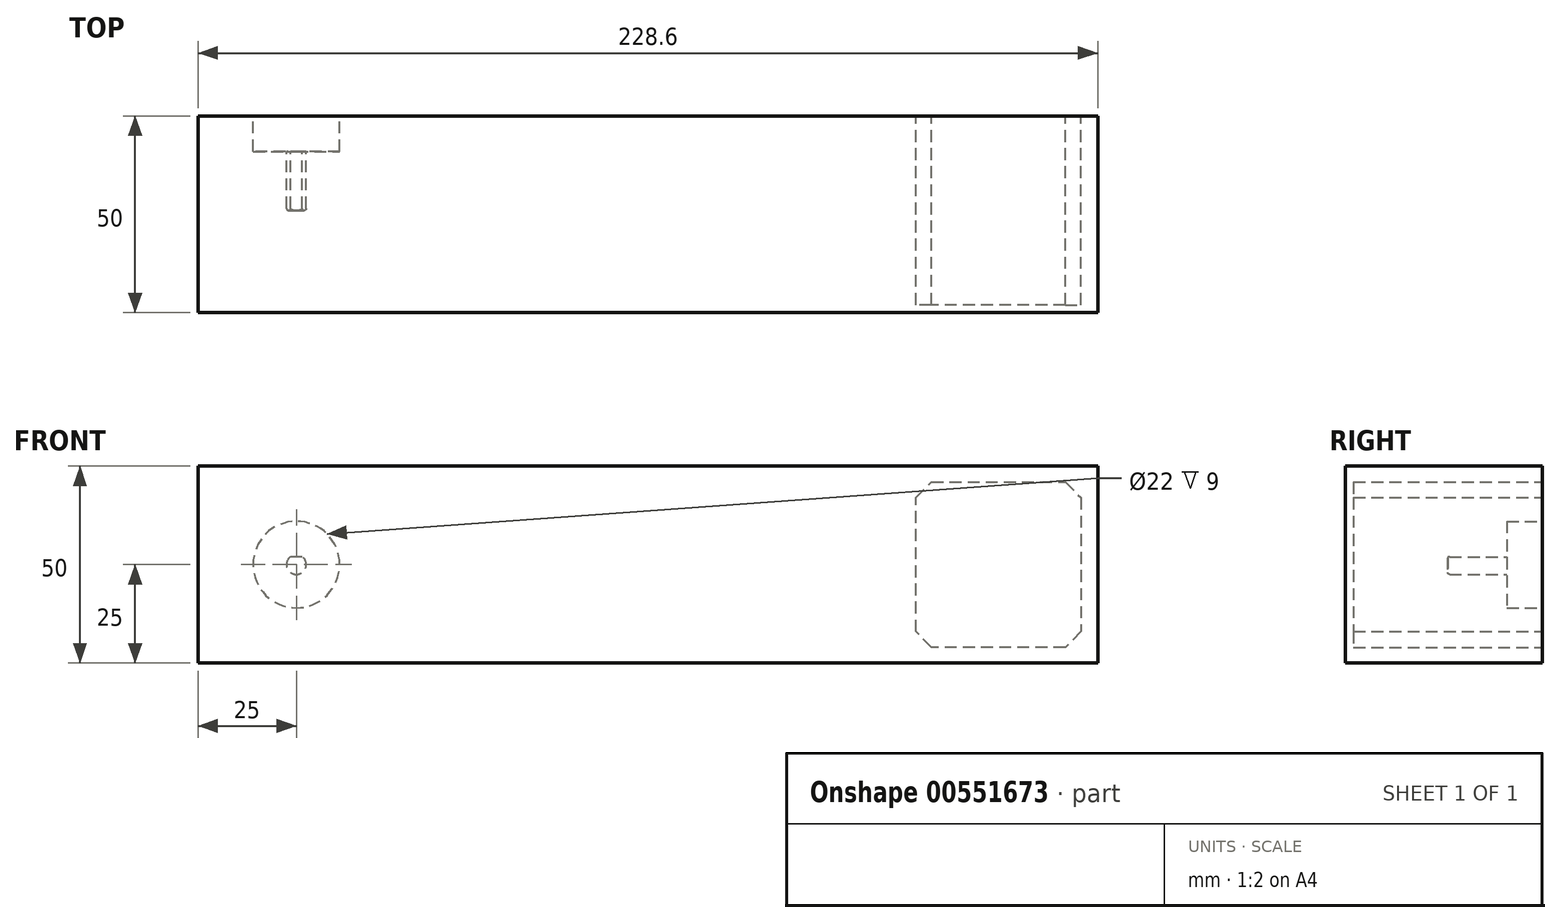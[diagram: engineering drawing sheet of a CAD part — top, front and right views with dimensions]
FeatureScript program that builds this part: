
annotation { "Feature Type Name" : "Feature", "Feature Type Description" : "" }
export const myFeature = defineFeature(function(context is Context, id is Id, definition is map)
    precondition{}
    {
        {
            var Q0;
            Q0=qCreatedBy(makeId("Front.planeOp"),FACE);
            var sketch = newSketch(context, id + "F0", { "sketchPlane" : qUnion([Q0])});
            skLineSegment(sketch, "E0.bottom", {"start": v(-114.3, -25) * mm, "end": v(114.3, -25) * mm});
            skLineSegment(sketch, "E0.top", {"start": v(-114.3, 25) * mm, "end": v(114.3, 25) * mm});
            skLineSegment(sketch, "E0.left", {"start": v(-114.3, -25) * mm, "end": v(-114.3, 25) * mm});
            skLineSegment(sketch, "E0.right", {"start": v(114.3, -25) * mm, "end": v(114.3, 25) * mm});
            skPoint(sketch, "E0.middle", {"position": v(0, 0) * mm});
            skSolve(sketch);
        }
        {
            var Q0;
            Q0=qSketchRegion(id+"F0",true);
            extrude(context, id + "F1", {"entities" : qUnion([Q0]), "depth" : 50 * mm, "offsetDistance" : 25 * mm});
        }
        {
            var Q0;
            Q0=makeQuery(id+"F1.opExtrude","CAP_FACE",FACE,{"disambiguationData":[OSD([sQuery(id+"F0.wireOp",EDGE,"E0.bottom"),sQuery(id+"F0.wireOp",EDGE,"E0.top"),sQuery(id+"F0.wireOp",EDGE,"E0.left"),sQuery(id+"F0.wireOp",EDGE,"E0.right")])],"isStart":true});
            var sketch = newSketch(context, id + "F2", { "sketchPlane" : qUnion([Q0])});
            skLineSegment(sketch, "E1", {"start": v(-110.06, 17) * mm, "end": v(-110.06, -17) * mm});
            skLineSegment(sketch, "E2", {"start": v(-110.06, -17) * mm, "end": v(-106.06, -21) * mm});
            skLineSegment(sketch, "E3", {"start": v(-106.06, -21) * mm, "end": v(-72.06, -21) * mm});
            skLineSegment(sketch, "E4", {"start": v(-72.06, -21) * mm, "end": v(-68.06, -17) * mm});
            skLineSegment(sketch, "E5", {"start": v(-68.06, -17) * mm, "end": v(-68.06, 17) * mm});
            skLineSegment(sketch, "E6", {"start": v(-68.06, 17) * mm, "end": v(-72.06, 21) * mm});
            skLineSegment(sketch, "E7", {"start": v(-72.06, 21) * mm, "end": v(-106.06, 21) * mm});
            skLineSegment(sketch, "E8", {"start": v(-106.06, 21) * mm, "end": v(-110.06, 17) * mm});
            skLineSegment(sketch, "E9", {"start": v(-101.08, 25) * mm, "end": v(-101.08, 21) * mm, "construction": true});
            skLineSegment(sketch, "E10", {"start": v(-89.06, -21) * mm, "end": v(-89.06, -25) * mm, "construction": true});
            skSolve(sketch);
        }
        {
            var Q0;
            Q0=qSketchRegion(id+"F2",true);
            extrude(context, id + "F3", {"entities" : qUnion([Q0]), "operationType" : NewBodyOperationType.REMOVE, "oppositeDirection" : true, "depth" : 48 * mm, "offsetDistance" : 25 * mm});
        }
        {
            var Q0;
            Q0=makeQuery(id+"F1.opExtrude","CAP_FACE",FACE,{"disambiguationData":[OSD([sQuery(id+"F0.wireOp",EDGE,"E0.bottom"),sQuery(id+"F0.wireOp",EDGE,"E0.top"),sQuery(id+"F0.wireOp",EDGE,"E0.left"),sQuery(id+"F0.wireOp",EDGE,"E0.right")])],"isStart":true});
            var sketch = newSketch(context, id + "F4", { "sketchPlane" : qUnion([Q0])});
            skCircle(sketch, "E11", {"center": v(89.3, 0) * mm, "radius": 11 * mm});
            skSolve(sketch);
        }
        {
            var Q0;
            Q0=qSketchRegion(id+"F4",true);
            extrude(context, id + "F5", {"entities" : qUnion([Q0]), "operationType" : NewBodyOperationType.REMOVE, "oppositeDirection" : true, "depth" : 9 * mm, "offsetDistance" : 25 * mm});
        }
        {
            var Q0;
            Q0=makeQuery(id+"F5.boolean.opBoolean","COPY",FACE,{"derivedFrom":makeQuery(id+"F5.opExtrude","CAP_FACE",FACE,{"disambiguationData":[OSD([sQuery(id+"F4.wireOp",EDGE,"E11")])],"isStart":false})});
            var sketch = newSketch(context, id + "F6", { "sketchPlane" : qUnion([Q0])});
            skArc(sketch, "E12", {"start": v(87.8, 2) * mm, "mid": v(89.3, -2.5) * mm, "end": v(90.8, 2) * mm});
            skLineSegment(sketch, "E13", {"start": v(87.8, 2) * mm, "end": v(90.8, 2) * mm});
            skSolve(sketch);
        }
        {
            var Q0;
            Q0=qSketchRegion(id+"F6",true);
            extrude(context, id + "F7", {"entities" : qUnion([Q0]), "operationType" : NewBodyOperationType.REMOVE, "oppositeDirection" : true, "depth" : 15 * mm, "offsetDistance" : 25 * mm});
        }
        {
            var Q0;
            Q0=makeQuery(id+"F7.boolean.opBoolean","COPY",EDGE,{"derivedFrom":makeQuery(id+"F7.opExtrude","CAP_EDGE",EDGE,{"disambiguationData":[OSD([sQuery(id+"F6.wireOp",EDGE,"E12")])],"isStart":false})});
            fillet(context, id + "F8", {"entities" : qUnion([Q0]), "radius" : .5 * mm, "tangentPropagation" : true, "allowEdgeOverflow" : false});
        }
    });
